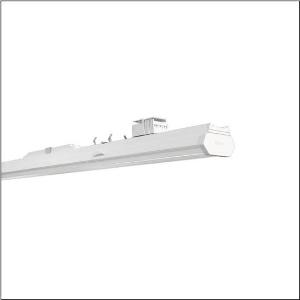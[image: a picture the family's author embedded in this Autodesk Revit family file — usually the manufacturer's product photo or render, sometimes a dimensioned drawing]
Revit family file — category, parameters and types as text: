
# Revit family: licross_r__21_protected_mo_51td12vn455g_01ce
name_source: partatom
category: Lighting Fixtures
units: mm (PartAtom-declared; Revit-internal decimal feet)

## family parameters
Cut with Voids When Loaded = No
Host = Face
Light Source = No
Part Type = Normal
Room Calculation Point = No
Round Connector Dimension = Use Diameter
Shared = No

## types (1)
- --- (1 x LED, 5500 lm, 29.7 W, 4000K)
    Apparent Load = 30 VA
    CIE Flux Codes = 73 92 98 99 100
    Color Rendering = 80
    Color Temperature = 4000K
    Default Elevation = 1800 mm
    Description = Licross® 21 Protected MO, luminaire insert, of sheet steel, galvanised, coil coated, white, length: 1.500mm, width: 66mm, height: 67mm, LED rated luminous flux: 5.500lm, light colour: 840, SDCM (Standard Deviation of Colour Matching)MacAdam ≤ 2 SDCM (initial), control gear: DALI 2, CLO, with plug, 5-pole, with phase selection, mains connection: 220..240V, AC, 50/60Hz, start of lifetime: 30W, end of service life: 33W, internal wiring halogen-free, primary optical cover: cover, of PMMA, light emission: direct distribution, primary light characteristic: symmetric, protection rating (complete): IP54, insulation class (complete): insulation class I (protective earthing), certification: CE, ENEC, VDE, UKCA, protection symbol: D if used in an environment with non-conductive dust loads with corresponding accessories, impact resistance: IK06, permissible ambient temperature for indoor applications: -25..+40°C, corresponds to IFS (International Featured Standards) requirements for safety and quality in the food industry, reducing of maximum allowable ambient temperature of 5°C with ceiling mounting, LABS conformity tested according to VDMA 24364:2018-05, packaging unit: 1 piece
    Height = 114 mm
    Lamp = 1 x LED
    Lamp Light Flux = 5500 lm
    Lamp Power = 29.7 W
    Lamp count = 1
    Length = 1500 mm
    Luminous efficacy = 185 lm/W
    Manufacturer = Siteco
    ModVariant = No
    Model = 51TD12VN455G
    Mounting Place = Ceiling
    Mounting Type = Pendant
    Number of Poles = 1
    OnlyDefault = Yes
    Power Factor = 1
    Product Name = Licross® 21 Protected MO
    Product group = luminaire insert | ceiling pendant
    ProductGroupID = 901
    Protection Class = Protection class I
    Protection Degree = IP 54
    RLX_Detail_Level = 1
    RLX_Emergency_Light_Flux = 0 lm
    RLX_Emergency_Type = 0
    RLX_Emergency_Type_DB = No
    RlxData = <blob elided: 31621 chars, md5=2bc3c1b4>
    Socket = socket
    Standby Power = 0 W
    System Light Flux = 5500 lm
    System Power = 30 W
    Type Comments = factory setting: luminous flux: 100 % | dim-lin: 254 | 200 mA
    Type Image = l_1256145.jpg
    URL = http://relux.com
    VarID = @adj_008373
    Voltage = 0 V
    Weight = 0.00 kg
    Width = 120 mm

## geometry (parser evidence)
native form markers: Blend x4, Sweep x11
no freeform markers — native parametric forms only
